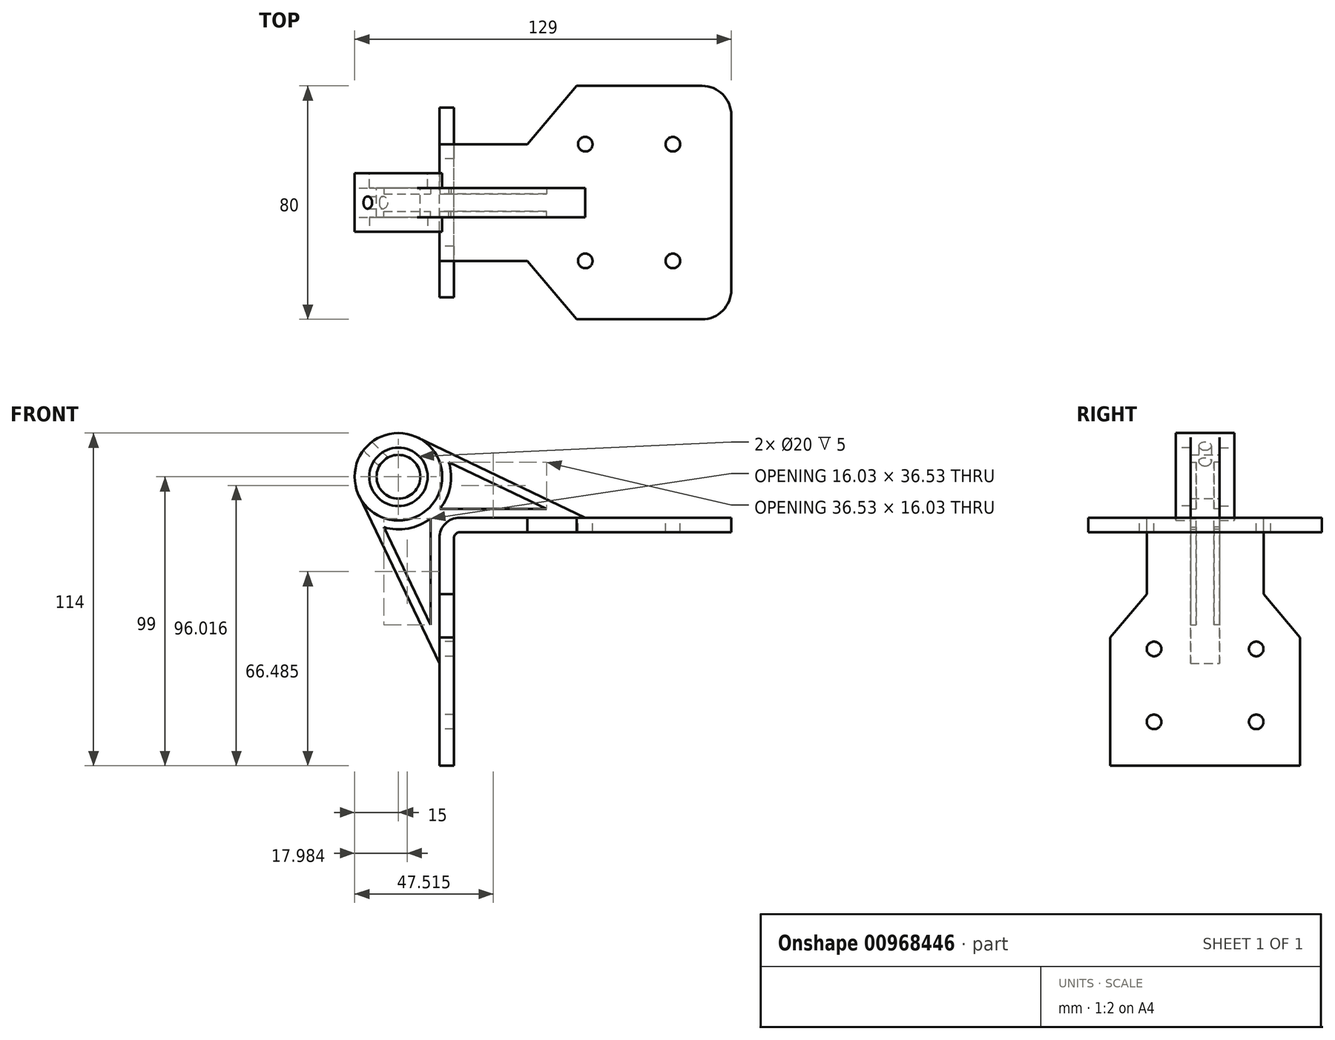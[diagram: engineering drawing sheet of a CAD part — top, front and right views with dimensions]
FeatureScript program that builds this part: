
annotation { "Feature Type Name" : "Feature", "Feature Type Description" : "" }
export const myFeature = defineFeature(function(context is Context, id is Id, definition is map)
    precondition{}
    {
        {
            var Q0;
            Q0=qCreatedBy(makeId("Front.planeOp"),FACE);
            var sketch = newSketch(context, id + "F0", { "sketchPlane" : qUnion([Q0])});
            skLineSegment(sketch, "E0", {"start": v(0, -85) * mm, "end": v(0, -7) * mm});
            skLineSegment(sketch, "E1", {"start": v(7, 0) * mm, "end": v(100, 0) * mm});
            skPoint(sketch, "E2.visualSharp", {"position": v(0, 0) * mm});
            skArc(sketch, "E2.filletArc", {"start": v(7, 0) * mm, "mid": v(2.05, -2.05) * mm, "end": v(0, -7) * mm});
            skLineSegment(sketch, "E3.0", {"start": v(7, -5) * mm, "end": v(100, -5) * mm});
            skArc(sketch, "E3.1", {"start": v(7, -5) * mm, "mid": v(5.59, -5.59) * mm, "end": v(5, -7) * mm});
            skLineSegment(sketch, "E3.2", {"start": v(5, -85) * mm, "end": v(5, -7) * mm});
            skLineSegment(sketch, "E4", {"start": v(100, 0) * mm, "end": v(100, -5) * mm});
            skLineSegment(sketch, "E5", {"start": v(0, -85) * mm, "end": v(5, -85) * mm});
            skCircle(sketch, "E6", {"center": v(-14, 14) * mm, "radius": 15 * mm});
            skCircle(sketch, "E7", {"center": v(-14, 14) * mm, "radius": 10 * mm});
            skCircle(sketch, "E8", {"center": v(-14, 14) * mm, "radius": 7.5 * mm});
            skLineSegment(sketch, "E9", {"start": v(-27.53, 7.52) * mm, "end": v(0, -50) * mm});
            skLineSegment(sketch, "E10", {"start": v(-7.52, 27.53) * mm, "end": v(50, 0) * mm});
            skLineSegment(sketch, "E11", {"start": v(-19.03, -3.28) * mm, "end": v(-3, -36.78) * mm});
            skLineSegment(sketch, "E12", {"start": v(-3, -36.78) * mm, "end": v(-3, -0.25) * mm});
            skLineSegment(sketch, "E13", {"start": v(3.28, 19.03) * mm, "end": v(36.78, 3) * mm});
            skLineSegment(sketch, "E14", {"start": v(36.78, 3) * mm, "end": v(0.25, 3) * mm});
            skArc(sketch, "E15", {"start": v(3.28, 19.03) * mm, "mid": v(3.69, 10.65) * mm, "end": v(0.25, 3) * mm});
            skArc(sketch, "E16", {"start": v(-3, -0.25) * mm, "mid": v(-10.65, -3.69) * mm, "end": v(-19.03, -3.28) * mm});
            skLineSegment(sketch, "E17", {"start": v(-14, 14) * mm, "end": v(-24.6, 24.6) * mm, "construction": true});
            skSolve(sketch);
        }
        {
            var Q0;
            Q0=sQuery(id+"F0.wireOp",EDGE,"E17");
            var Q1;
            Q1=sQuery(id+"F0.wireOp",VERTEX,"E17.end");
            cPlane(context, id + "F1", {"entities" : qUnion([Q0, Q1]), "cplaneType" : CPlaneType.LINE_POINT, "offset" : 25 * mm, "width" : 150 * mm, "height" : 150 * mm});
        }
        {
            var Q0;
            Q0=qCreatedBy(makeId("Right.planeOp"),FACE);
            var sketch = newSketch(context, id + "F2", { "sketchPlane" : qUnion([Q0])});
            skLineSegment(sketch, "E18", {"start": v(-20, 0) * mm, "end": v(-20, -26.16) * mm});
            skLineSegment(sketch, "E19", {"start": v(-20, -26.16) * mm, "end": v(-32.5, -41.06) * mm});
            skLineSegment(sketch, "E20", {"start": v(-40, -85) * mm, "end": v(-40, 0) * mm});
            skLineSegment(sketch, "E21", {"start": v(-40, 0) * mm, "end": v(-20, 0) * mm});
            skLineSegment(sketch, "E22", {"start": v(-32.5, -41.06) * mm, "end": v(-32.5, -85) * mm});
            skLineSegment(sketch, "E23", {"start": v(-32.5, -85) * mm, "end": v(-40, -85) * mm});
            skPoint(sketch, "E24.orphan", {"position": v(-40, -50) * mm});
            skSolve(sketch);
        }
        {
            var Q0;
            Q0=qCreatedBy(makeId("Top.planeOp"),FACE);
            var sketch = newSketch(context, id + "F3", { "sketchPlane" : qUnion([Q0])});
            skLineSegment(sketch, "E25", {"start": v(0, -20) * mm, "end": v(30.22, -20) * mm});
            skLineSegment(sketch, "E26", {"start": v(30.22, -20) * mm, "end": v(47, -40) * mm});
            skLineSegment(sketch, "E27", {"start": v(47, -40) * mm, "end": v(0, -40) * mm});
            skLineSegment(sketch, "E28", {"start": v(0, -40) * mm, "end": v(0, -20) * mm});
            skSolve(sketch);
        }
        {
            var Q0;
            {var subQ3=sQuery(id+"F0.wireOp",EDGE,"E2.filletArc");Q0=makeQuery(id+"F0.imprint","IMPRINT",FACE,{"disambiguationData":[TD([[makeQuery(id+"F0.imprint","IMPRINT",EDGE,{"derivedFrom":subQ3}),1.0]])]});}
            extrude(context, id + "F4", {"entities" : qUnion([Q0]), "depth" : 40 * mm, "offsetDistance" : 25 * mm});
        }
        {
            var Q0;
            Q0=makeQuery(id+"F2.imprint","IMPRINT",FACE,{"disambiguationData":[TD([[makeQuery(id+"F2.imprint","IMPRINT",EDGE,{"derivedFrom":sQuery(id+"F2.wireOp",EDGE,"E18")}),-1.0]])]});
            extrude(context, id + "F5", {"entities" : qUnion([Q0]), "operationType" : NewBodyOperationType.REMOVE, "depth" : 10 * mm, "offsetDistance" : 25 * mm});
        }
        {
            var Q0;
            Q0=makeQuery(id+"F3.imprint","IMPRINT",FACE,{"disambiguationData":[TD([[makeQuery(id+"F3.imprint","IMPRINT",EDGE,{"derivedFrom":sQuery(id+"F3.wireOp",EDGE,"E25")}),-1.0]])]});
            extrude(context, id + "F6", {"entities" : qUnion([Q0]), "operationType" : NewBodyOperationType.REMOVE, "oppositeDirection" : true, "depth" : 10 * mm, "offsetDistance" : 25 * mm});
        }
        {
            var Q0;
            Q0=makeQuery(id+"F5.boolean.opBoolean","COPY",EDGE,{"derivedFrom":makeQuery(id+"F5.opExtrude","SWEPT_EDGE",EDGE,{"disambiguationData":[OSD([sQuery(id+"F2.wireOp",EDGE,"E22"),sQuery(id+"F2.wireOp",EDGE,"E23")])]})});
            var Q1;
            Q1=makeQuery(id+"F4.opExtrude","CAP_EDGE",EDGE,{"disambiguationData":[OSD([sQuery(id+"F0.wireOp",EDGE,"E4")])],"isStart":false});
            fillet(context, id + "F7", {"entities" : qUnion([Q0, Q1]), "radius" : 10 * mm, "tangentPropagation" : true, "allowEdgeOverflow" : false});
        }
        {
            var Q0;
            Q0=qCreatedBy(makeId("Right.planeOp"),FACE);
            var sketch = newSketch(context, id + "F8", { "sketchPlane" : qUnion([Q0])});
            skLineSegment(sketch, "E29", {"start": v(-17.5, -45) * mm, "end": v(-17.5, -70) * mm, "construction": true});
            skCircle(sketch, "E30", {"center": v(-17.5, -45) * mm, "radius": 2.5 * mm});
            skCircle(sketch, "E31", {"center": v(-17.5, -70) * mm, "radius": 2.5 * mm});
            skSolve(sketch);
        }
        {
            var Q0;
            Q0=qCreatedBy(makeId("Top.planeOp"),FACE);
            var sketch = newSketch(context, id + "F9", { "sketchPlane" : qUnion([Q0])});
            skLineSegment(sketch, "E32", {"start": v(80, -20) * mm, "end": v(50, -20) * mm, "construction": true});
            skCircle(sketch, "E33", {"center": v(80, -20) * mm, "radius": 2.5 * mm});
            skCircle(sketch, "E34", {"center": v(50, -20) * mm, "radius": 2.5 * mm});
            skSolve(sketch);
        }
        {
            var Q0;
            Q0=makeQuery(id+"F8.imprint","IMPRINT",FACE,{"disambiguationData":[TD([[makeQuery(id+"F8.imprint","IMPRINT",EDGE,{"derivedFrom":sQuery(id+"F8.wireOp",EDGE,"E31")}),1.0]])]});
            var Q1;
            Q1=makeQuery(id+"F8.imprint","IMPRINT",FACE,{"disambiguationData":[TD([[makeQuery(id+"F8.imprint","IMPRINT",EDGE,{"derivedFrom":sQuery(id+"F8.wireOp",EDGE,"E30")}),1.0]])]});
            extrude(context, id + "F10", {"entities" : qUnion([Q0, Q1]), "operationType" : NewBodyOperationType.REMOVE, "endBound" : BoundingType.THROUGH_ALL, "depth" : 25 * mm, "offsetDistance" : 25 * mm});
        }
        {
            var Q0;
            Q0=makeQuery(id+"F9.imprint","IMPRINT",FACE,{"disambiguationData":[TD([[makeQuery(id+"F9.imprint","IMPRINT",EDGE,{"derivedFrom":sQuery(id+"F9.wireOp",EDGE,"E34")}),1.0]])]});
            var Q1;
            Q1=makeQuery(id+"F9.imprint","IMPRINT",FACE,{"disambiguationData":[TD([[makeQuery(id+"F9.imprint","IMPRINT",EDGE,{"derivedFrom":sQuery(id+"F9.wireOp",EDGE,"E33")}),1.0]])]});
            extrude(context, id + "F11", {"entities" : qUnion([Q0, Q1]), "operationType" : NewBodyOperationType.REMOVE, "endBound" : BoundingType.THROUGH_ALL, "oppositeDirection" : true, "depth" : 25 * mm, "offsetDistance" : 25 * mm});
        }
        {
            var Q0;
            {var subQ1=sQuery(id+"F0.wireOp",EDGE,"E2.filletArc");Q0=makeQuery(id+"F0.imprint","IMPRINT",FACE,{"disambiguationData":[TD([[makeQuery(id+"F0.imprint","IMPRINT",EDGE,{"derivedFrom":subQ1}),-1.0]])]});}
            extrude(context, id + "F12", {"entities" : qUnion([Q0]), "operationType" : NewBodyOperationType.ADD, "depth" : 5 * mm, "offsetDistance" : 25 * mm});
        }
        {
            var Q0;
            Q0=makeQuery(id+"F0.imprint","IMPRINT",FACE,{"disambiguationData":[TD([[makeQuery(id+"F0.imprint","IMPRINT",EDGE,{"derivedFrom":sQuery(id+"F0.wireOp",EDGE,"E13")}),-1.0]])]});
            var Q1;
            Q1=makeQuery(id+"F0.imprint","IMPRINT",FACE,{"disambiguationData":[TD([[makeQuery(id+"F0.imprint","IMPRINT",EDGE,{"derivedFrom":sQuery(id+"F0.wireOp",EDGE,"E11")}),1.0]])]});
            extrude(context, id + "F13", {"entities" : qUnion([Q0, Q1]), "operationType" : NewBodyOperationType.ADD, "depth" : 3 * mm, "offsetDistance" : 25 * mm});
        }
        {
            var Q0;
            Q0=makeQuery(id+"F0.imprint","IMPRINT",FACE,{"disambiguationData":[TD([[makeQuery(id+"F0.imprint","IMPRINT",EDGE,{"derivedFrom":sQuery(id+"F0.wireOp",EDGE,"E7")}),-1.0]])]});
            var Q1;
            Q1=makeQuery(id+"F0.imprint","IMPRINT",FACE,{"disambiguationData":[TD([[makeQuery(id+"F0.imprint","IMPRINT",EDGE,{"derivedFrom":sQuery(id+"F0.wireOp",EDGE,"E7")}),1.0]])]});
            extrude(context, id + "F14", {"entities" : qUnion([Q0, Q1]), "operationType" : NewBodyOperationType.ADD, "depth" : 10 * mm, "offsetDistance" : 25 * mm});
        }
        {
            var Q0;
            Q0=makeQuery(id+"F14.opExtrude","CAP_FACE",FACE,{"disambiguationData":[OSD([sQuery(id+"F0.wireOp",EDGE,"E6"),sQuery(id+"F0.wireOp",EDGE,"E8")])],"isStart":false});
            var sketch = newSketch(context, id + "F15", { "sketchPlane" : qUnion([Q0])});
            skCircle(sketch, "E35.0", {"center": v(-14, 14) * mm, "radius": 10 * mm});
            skSolve(sketch);
        }
        {
            var Q0;
            Q0=makeQuery(id+"F15.imprint","IMPRINT",FACE,{"disambiguationData":[TD([[makeQuery(id+"F15.imprint","IMPRINT",EDGE,{"derivedFrom":sQuery(id+"F15.wireOp",EDGE,"E35.0")}),1.0]])]});
            extrude(context, id + "F16", {"entities" : qUnion([Q0]), "operationType" : NewBodyOperationType.REMOVE, "oppositeDirection" : true, "depth" : 5 * mm, "offsetDistance" : 25 * mm});
        }
        {
            var Q0;
            Q0=makeQuery(id+"F4.opExtrude","SWEPT_BODY",BODY,{"disambiguationData":[OSD([sQuery(id+"F0.wireOp",EDGE,"E0"),sQuery(id+"F0.wireOp",EDGE,"E1"),sQuery(id+"F0.wireOp",EDGE,"E2.filletArc"),sQuery(id+"F0.wireOp",EDGE,"E3.0"),sQuery(id+"F0.wireOp",EDGE,"E3.1"),sQuery(id+"F0.wireOp",EDGE,"E3.2"),sQuery(id+"F0.wireOp",EDGE,"E4"),sQuery(id+"F0.wireOp",EDGE,"E5")])]});
            var Q1;
            Q1=qCreatedBy(makeId("Front.planeOp"),FACE);
            mirror(context, id + "F17", {"operationType" : NewBodyOperationType.ADD, "entities" : qUnion([Q0]), "mirrorPlane" : qUnion([Q1])});
        }
        {
            var Q0;
            Q0=qCreatedBy(id+"F1.planeOp",FACE);
            var sketch = newSketch(context, id + "F18", { "sketchPlane" : qUnion([Q0])});
            skPoint(sketch, "E36.0", {"position": v(0, 0) * mm});
            skSolve(sketch);
        }
        {
            var Q0;
            Q0=sQuery(id+"F18.wireOp",VERTEX,"E36.0");
            var Q1;
            Q1=makeQuery(id+"F4.opExtrude","SWEPT_BODY",BODY,{"disambiguationData":[OSD([sQuery(id+"F0.wireOp",EDGE,"E0"),sQuery(id+"F0.wireOp",EDGE,"E1"),sQuery(id+"F0.wireOp",EDGE,"E2.filletArc"),sQuery(id+"F0.wireOp",EDGE,"E3.0"),sQuery(id+"F0.wireOp",EDGE,"E3.1"),sQuery(id+"F0.wireOp",EDGE,"E3.2"),sQuery(id+"F0.wireOp",EDGE,"E4"),sQuery(id+"F0.wireOp",EDGE,"E5")])]});
            hole(context, id + "F19", {"style" : HoleStyle.SIMPLE, "endStyle" : HoleEndStyle.BLIND, "standardTappedOrClearance" : lookupTablePath({ "standard" : "ISO", "engagement" : "75%", "pitch" : "0.8 mm", "size" : "M5", "type" : "Tapped" }), "standardBlindInLast" : lookupTablePath({ "standard" : "ISO", "fit" : "Normal", "engagement" : "75%", "pitch" : "0.8 mm", "size" : "M5", "type" : "Clearance & tapped" }), "holeDiameter" : 4.2 * mm, "majorDiameter" : 5 * mm, "showTappedDepth" : true, "holeDepth" : 10 * mm, "isTappedThrough" : true, "tappedDepth" : 10 * mm, "tapClearance" : 0, "startFromSketch" : true, "locations" : qUnion([Q0]), "scope" : qUnion([Q1])});
        }
    });
